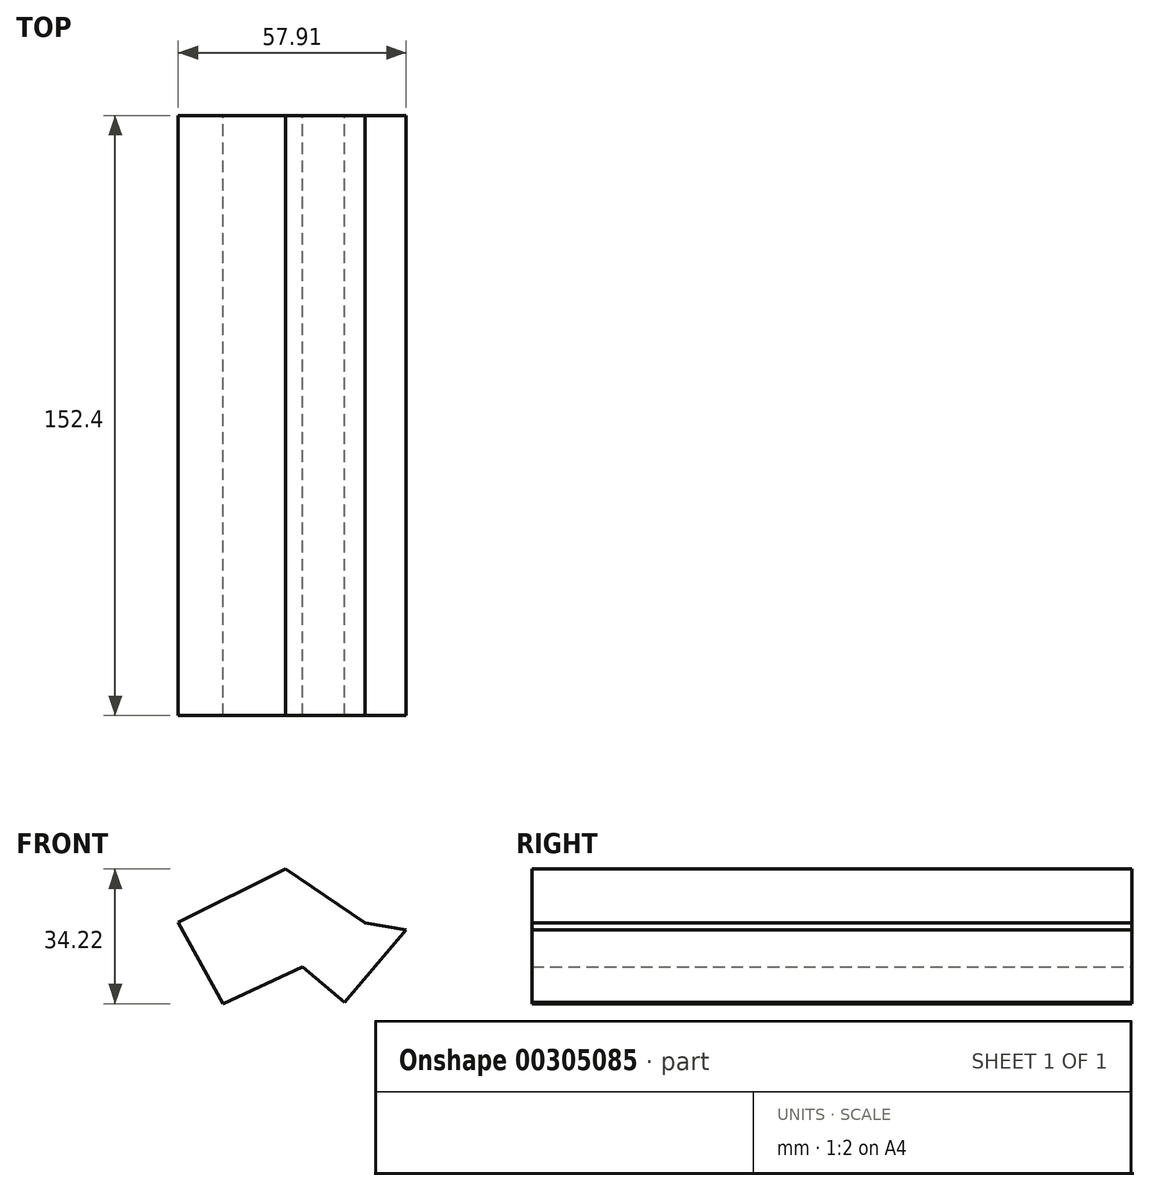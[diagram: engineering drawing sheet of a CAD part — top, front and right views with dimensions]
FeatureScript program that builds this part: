
annotation { "Feature Type Name" : "Feature", "Feature Type Description" : "" }
export const myFeature = defineFeature(function(context is Context, id is Id, definition is map)
    precondition{}
    {
        {
            var Q0;
            Q0=qCreatedBy(makeId("Front.planeOp"),FACE);
            var sketch = newSketch(context, id + "F0", { "sketchPlane" : qUnion([Q0])});
            skLineSegment(sketch, "E0", {"start": v(-20.34, 9.04) * mm, "end": v(6.95, 22.6) * mm});
            skLineSegment(sketch, "E1", {"start": v(6.95, 22.6) * mm, "end": v(27.17, 8.9) * mm});
            skLineSegment(sketch, "E2", {"start": v(27.17, 8.9) * mm, "end": v(37.57, 7.16) * mm});
            skLineSegment(sketch, "E3", {"start": v(37.57, 7.16) * mm, "end": v(21.97, -11.32) * mm});
            skLineSegment(sketch, "E4", {"start": v(21.97, -11.32) * mm, "end": v(11.25, -2.27) * mm});
            skLineSegment(sketch, "E5", {"start": v(11.25, -2.27) * mm, "end": v(-8.93, -11.61) * mm});
            skLineSegment(sketch, "E6", {"start": v(-8.93, -11.61) * mm, "end": v(-20.34, 9.04) * mm});
            skSolve(sketch);
        }
        {
            var Q0;
            Q0=makeQuery(id+"F0.imprint","IMPRINT",FACE,{"disambiguationData":[TD([[makeQuery(id+"F0.imprint","IMPRINT",EDGE,{"derivedFrom":sQuery(id+"F0.wireOp",EDGE,"E0")}),-1.0]])]});
            extrude(context, id + "F1", {"entities" : qUnion([Q0]), "depth" : 152.4 * mm});
        }
    });
